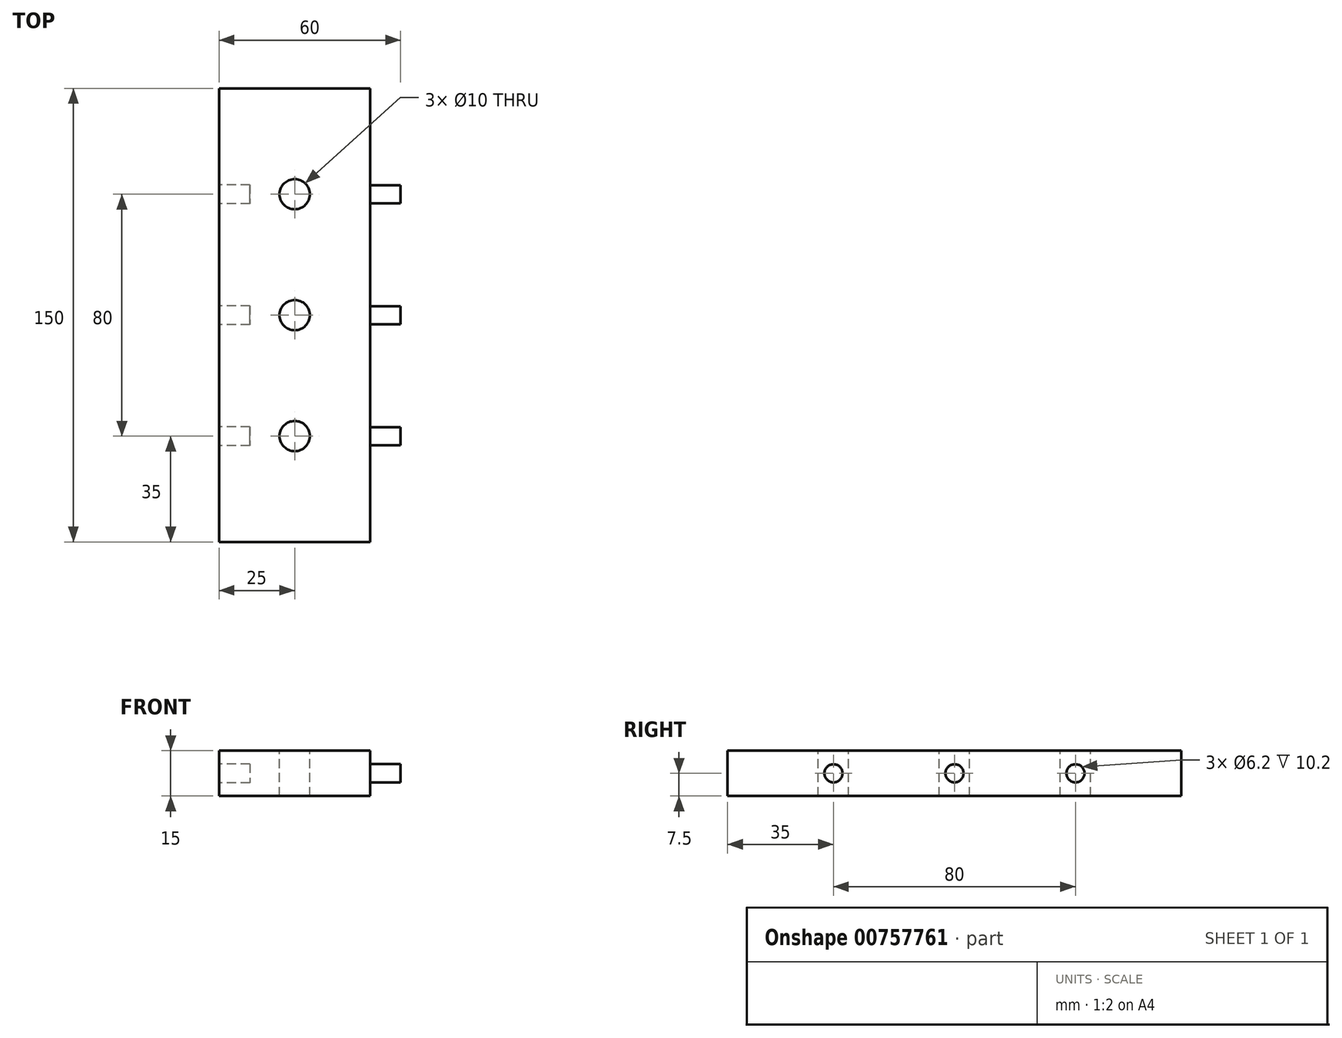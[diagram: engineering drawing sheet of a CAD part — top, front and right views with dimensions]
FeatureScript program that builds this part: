
annotation { "Feature Type Name" : "Feature", "Feature Type Description" : "" }
export const myFeature = defineFeature(function(context is Context, id is Id, definition is map)
    precondition{}
    {
        {
            var Q0;
            Q0=qCreatedBy(makeId("Top.planeOp"),FACE);
            var sketch = newSketch(context, id + "F0", { "sketchPlane" : qUnion([Q0])});
            skLineSegment(sketch, "E0.bottom", {"start": v(25, 75) * mm, "end": v(-25, 75) * mm});
            skLineSegment(sketch, "E0.top", {"start": v(25, -75) * mm, "end": v(-25, -75) * mm});
            skLineSegment(sketch, "E0.left", {"start": v(25, 75) * mm, "end": v(25, -75) * mm});
            skLineSegment(sketch, "E0.right", {"start": v(-25, 75) * mm, "end": v(-25, -75) * mm});
            skPoint(sketch, "E0.middle", {"position": v(0, 0) * mm});
            skSolve(sketch);
        }
        {
            var Q0;
            Q0=makeQuery(id+"F0.imprint","IMPRINT",FACE,{"disambiguationData":[TD([[makeQuery(id+"F0.imprint","IMPRINT",EDGE,{"derivedFrom":sQuery(id+"F0.wireOp",EDGE,"E0.bottom")}),1.0]])]});
            extrude(context, id + "F1", {"entities" : qUnion([Q0]), "depth" : 15 * mm, "offsetDistance" : 25 * mm});
        }
        {
            var Q0;
            Q0=makeQuery(id+"F1.opExtrude","CAP_FACE",FACE,{"disambiguationData":[OSD([sQuery(id+"F0.wireOp",EDGE,"E0.bottom"),sQuery(id+"F0.wireOp",EDGE,"E0.top"),sQuery(id+"F0.wireOp",EDGE,"E0.left"),sQuery(id+"F0.wireOp",EDGE,"E0.right")])],"isStart":false});
            var sketch = newSketch(context, id + "F2", { "sketchPlane" : qUnion([Q0])});
            skPoint(sketch, "E1", {"position": v(0, 40) * mm});
            skCircle(sketch, "E2", {"center": v(0, 40) * mm, "radius": 5 * mm});
            skCircle(sketch, "E3", {"center": v(0, 0) * mm, "radius": 5 * mm});
            skCircle(sketch, "E4", {"center": v(0, -40) * mm, "radius": 5 * mm});
            skSolve(sketch);
        }
        {
            var Q0;
            Q0=makeQuery(id+"F2.imprint","IMPRINT",FACE,{"disambiguationData":[TD([[makeQuery(id+"F2.imprint","IMPRINT",EDGE,{"derivedFrom":sQuery(id+"F2.wireOp",EDGE,"E2")}),1.0]])]});
            var Q1;
            Q1=makeQuery(id+"F2.imprint","IMPRINT",FACE,{"disambiguationData":[TD([[makeQuery(id+"F2.imprint","IMPRINT",EDGE,{"derivedFrom":sQuery(id+"F2.wireOp",EDGE,"E3")}),1.0]])]});
            var Q2;
            Q2=makeQuery(id+"F2.imprint","IMPRINT",FACE,{"disambiguationData":[TD([[makeQuery(id+"F2.imprint","IMPRINT",EDGE,{"derivedFrom":sQuery(id+"F2.wireOp",EDGE,"E4")}),1.0]])]});
            extrude(context, id + "F3", {"entities" : qUnion([Q0, Q1, Q2]), "operationType" : NewBodyOperationType.REMOVE, "oppositeDirection" : true, "depth" : 25 * mm, "offsetDistance" : 25 * mm});
        }
        {
            var Q0;
            Q0=makeQuery(id+"F1.opExtrude","SWEPT_FACE",FACE,{"disambiguationData":[OSD([sQuery(id+"F0.wireOp",EDGE,"E0.left")])]});
            var sketch = newSketch(context, id + "F4", { "sketchPlane" : qUnion([Q0])});
            skCircle(sketch, "E5", {"center": v(-40, 7.5) * mm, "radius": 3 * mm});
            skCircle(sketch, "E6", {"center": v(0, 7.5) * mm, "radius": 3 * mm});
            skCircle(sketch, "E7", {"center": v(40, 7.5) * mm, "radius": 3 * mm});
            skSolve(sketch);
        }
        {
            var Q0;
            Q0=makeQuery(id+"F4.imprint","IMPRINT",FACE,{"disambiguationData":[TD([[makeQuery(id+"F4.imprint","IMPRINT",EDGE,{"derivedFrom":sQuery(id+"F4.wireOp",EDGE,"E5")}),1.0]])]});
            var Q1;
            Q1=makeQuery(id+"F4.imprint","IMPRINT",FACE,{"disambiguationData":[TD([[makeQuery(id+"F4.imprint","IMPRINT",EDGE,{"derivedFrom":sQuery(id+"F4.wireOp",EDGE,"E6")}),1.0]])]});
            var Q2;
            Q2=makeQuery(id+"F4.imprint","IMPRINT",FACE,{"disambiguationData":[TD([[makeQuery(id+"F4.imprint","IMPRINT",EDGE,{"derivedFrom":sQuery(id+"F4.wireOp",EDGE,"E7")}),1.0]])]});
            extrude(context, id + "F5", {"entities" : qUnion([Q0, Q1, Q2]), "operationType" : NewBodyOperationType.ADD, "depth" : 10 * mm, "offsetDistance" : 25 * mm});
        }
        {
            var Q0;
            Q0=makeQuery(id+"F1.opExtrude","SWEPT_FACE",FACE,{"disambiguationData":[OSD([sQuery(id+"F0.wireOp",EDGE,"E0.right")])]});
            var sketch = newSketch(context, id + "F6", { "sketchPlane" : qUnion([Q0])});
            skCircle(sketch, "E8", {"center": v(-40, 7.5) * mm, "radius": 3.1 * mm});
            skCircle(sketch, "E9", {"center": v(40, 7.5) * mm, "radius": 3.1 * mm});
            skCircle(sketch, "E10", {"center": v(0, 7.5) * mm, "radius": 3.1 * mm});
            skSolve(sketch);
        }
        {
            var Q0;
            Q0=makeQuery(id+"F6.imprint","IMPRINT",FACE,{"disambiguationData":[TD([[makeQuery(id+"F6.imprint","IMPRINT",EDGE,{"derivedFrom":sQuery(id+"F6.wireOp",EDGE,"E8")}),1.0]])]});
            var Q1;
            Q1=makeQuery(id+"F6.imprint","IMPRINT",FACE,{"disambiguationData":[TD([[makeQuery(id+"F6.imprint","IMPRINT",EDGE,{"derivedFrom":sQuery(id+"F6.wireOp",EDGE,"E10")}),1.0]])]});
            var Q2;
            Q2=makeQuery(id+"F6.imprint","IMPRINT",FACE,{"disambiguationData":[TD([[makeQuery(id+"F6.imprint","IMPRINT",EDGE,{"derivedFrom":sQuery(id+"F6.wireOp",EDGE,"E9")}),1.0]])]});
            extrude(context, id + "F7", {"entities" : qUnion([Q0, Q1, Q2]), "operationType" : NewBodyOperationType.REMOVE, "oppositeDirection" : true, "depth" : 10.2 * mm, "offsetDistance" : 25 * mm});
        }
    });
